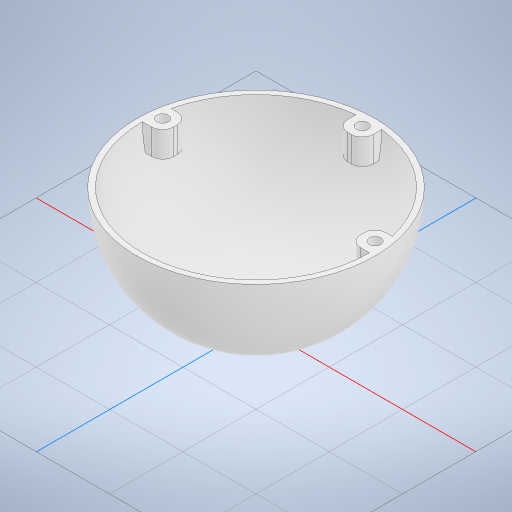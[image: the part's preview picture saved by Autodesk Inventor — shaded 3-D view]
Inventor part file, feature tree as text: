
AUTODESK INVENTOR PART (.ipt)
format: ipt  version: 2023 (Build 270158000, 158)  size: 338,432 bytes
history: native  units: mm
features: extrude x3, sketch x1, revolve x1, shell x1, delete_face x1, fillet x1
ambient origin geometry x8: Origin, YZ Plane, XZ Plane, XY Plane, X Axis, Y Axis, Z Axis, Center Point
bodies: Volumenkörper1 (feature_tree)
feature tree (8):
  sketch  "Skizze1"  dims[d0=65.0mm d1=90.0deg d2=65.0mm d3=7.0mm d4=7.0mm d5=7.0mm d6=7.0mm d13=10.0mm d14=0.0mm d15=1.5mm d16=7.0mm d17=0.0mm d20=7.0mm d21=7.0mm d22=32.5mm d23=3.2mm d24=3.2mm d25=3.2mm d26=5.0mm d27=0.0mm d28=3.0mm]
  revolve  "Umdrehung1"
  extrude  "Extrusion1"  TaperAngle=90.0deg  [1 undecoded]
  shell  "Wandung1"  Thickness=65.0mm
  extrude  "Extrusion2"  Depth=7.0mm
  delete_face  "Fläche löschen1"
  extrude  "Extrusion3"  Depth=7.0mm
  fillet  "Rundung1"  Radius=7.0mm
note: 1 required parameter value undecoded (feature->parameter linkage not recoverable at this tier; creation-order binding heuristic only, values carry confidence <= 0.55)
